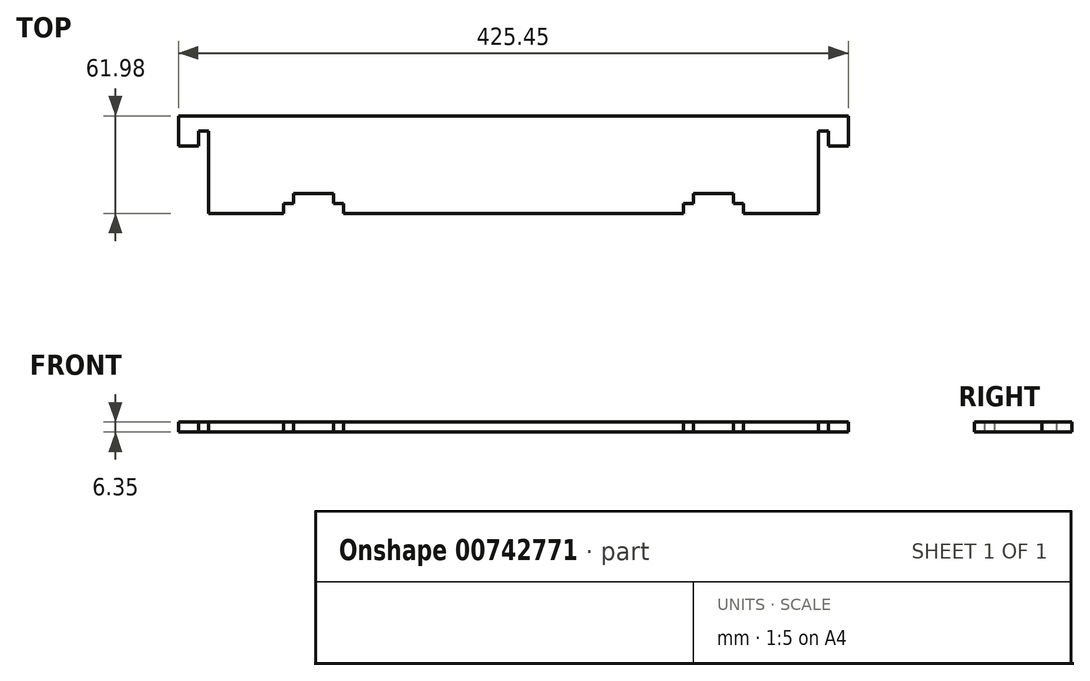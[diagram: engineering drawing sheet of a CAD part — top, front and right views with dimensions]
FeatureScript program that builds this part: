
annotation { "Feature Type Name" : "Feature", "Feature Type Description" : "" }
export const myFeature = defineFeature(function(context is Context, id is Id, definition is map)
    precondition{}
    {
        {
            var Q0;
            Q0=qCreatedBy(makeId("Top.planeOp"),FACE);
            var sketch = newSketch(context, id + "F0", { "sketchPlane" : qUnion([Q0])});
            skLineSegment(sketch, "E0.top", {"start": v(-116.14, -61.98) * mm, "end": v(-68.51, -61.98) * mm});
            skLineSegment(sketch, "E0.left", {"start": v(-116.14, 0) * mm, "end": v(-116.14, -61.98) * mm});
            skLineSegment(sketch, "E0.right", {"start": v(271.21, 0) * mm, "end": v(271.21, -61.98) * mm});
            skLineSegment(sketch, "E1.top", {"start": v(-68.51, -55.63) * mm, "end": v(-62.16, -55.63) * mm});
            skLineSegment(sketch, "E1.left", {"start": v(-68.51, -61.98) * mm, "end": v(-68.51, -55.63) * mm});
            skLineSegment(sketch, "E1.right", {"start": v(-30.41, -61.98) * mm, "end": v(-30.41, -55.63) * mm});
            skLineSegment(sketch, "E2.bottom", {"start": v(185.49, -55.63) * mm, "end": v(191.84, -55.63) * mm});
            skLineSegment(sketch, "E2.left", {"start": v(185.49, -55.63) * mm, "end": v(185.49, -61.98) * mm});
            skLineSegment(sketch, "E2.right", {"start": v(223.59, -55.63) * mm, "end": v(223.59, -61.98) * mm});
            skLineSegment(sketch, "E3.top", {"start": v(191.84, -49.28) * mm, "end": v(217.24, -49.28) * mm});
            skLineSegment(sketch, "E3.left", {"start": v(191.84, -55.63) * mm, "end": v(191.84, -49.28) * mm});
            skLineSegment(sketch, "E3.right", {"start": v(217.24, -55.63) * mm, "end": v(217.24, -49.28) * mm});
            skLineSegment(sketch, "E4.top", {"start": v(-62.16, -49.28) * mm, "end": v(-36.76, -49.28) * mm});
            skLineSegment(sketch, "E4.left", {"start": v(-62.16, -55.63) * mm, "end": v(-62.16, -49.28) * mm});
            skLineSegment(sketch, "E4.right", {"start": v(-36.76, -55.63) * mm, "end": v(-36.76, -49.28) * mm});
            skLineSegment(sketch, "E5.trimOffspring", {"start": v(-36.76, -55.63) * mm, "end": v(-30.41, -55.63) * mm});
            skLineSegment(sketch, "E6.trimOffspring", {"start": v(217.24, -55.63) * mm, "end": v(223.59, -55.63) * mm});
            skLineSegment(sketch, "E7.trimOffspring", {"start": v(223.59, -61.98) * mm, "end": v(271.21, -61.98) * mm});
            skLineSegment(sketch, "E8.trimOffspring", {"start": v(-116.14, 0) * mm, "end": v(271.21, 0) * mm});
            skLineSegment(sketch, "E9.trimOffspring", {"start": v(-30.41, -61.98) * mm, "end": v(185.49, -61.98) * mm});
            skSolve(sketch);
        }
        {
            var Q0;
            Q0=qSketchRegion(id+"F0",true);
            extrude(context, id + "F1", {"entities" : qUnion([Q0]), "depth" : 6.35 * mm, "offsetDistance" : 25.4 * mm});
        }
        {
            var Q0;
            Q0=makeQuery(id+"F1.opExtrude","CAP_FACE",FACE,{"disambiguationData":[OSD([sQuery(id+"F0.wireOp",EDGE,"E0.bottom"),sQuery(id+"F0.wireOp",EDGE,"E0.top"),sQuery(id+"F0.wireOp",EDGE,"E0.left"),sQuery(id+"F0.wireOp",EDGE,"E0.right"),sQuery(id+"F0.wireOp",EDGE,"E1.top"),sQuery(id+"F0.wireOp",EDGE,"E1.left"),sQuery(id+"F0.wireOp",EDGE,"E1.right"),sQuery(id+"F0.wireOp",EDGE,"E2.bottom"),sQuery(id+"F0.wireOp",EDGE,"E2.left"),sQuery(id+"F0.wireOp",EDGE,"E2.right"),sQuery(id+"F0.wireOp",EDGE,"E3.top"),sQuery(id+"F0.wireOp",EDGE,"E3.left"),sQuery(id+"F0.wireOp",EDGE,"E3.right"),sQuery(id+"F0.wireOp",EDGE,"E4.top"),sQuery(id+"F0.wireOp",EDGE,"E4.left"),sQuery(id+"F0.wireOp",EDGE,"E4.right"),sQuery(id+"F0.wireOp",EDGE,"E5.trimOffspring"),sQuery(id+"F0.wireOp",EDGE,"c7ddb3ed-293a-4f06-881b-95a2d0f9c08b.trimOffspring"),sQuery(id+"F0.wireOp",EDGE,"E6.trimOffspring"),sQuery(id+"F0.wireOp",EDGE,"E7.trimOffspring"),sQuery(id+"F0.wireOp",EDGE,"ymufXbJ0-fwJT-WBPx-Nqb6-yKuEAUtQnc4U.top"),sQuery(id+"F0.wireOp",EDGE,"ymufXbJ0-fwJT-WBPx-Nqb6-yKuEAUtQnc4U.left"),sQuery(id+"F0.wireOp",EDGE,"ymufXbJ0-fwJT-WBPx-Nqb6-yKuEAUtQnc4U.right"),sQuery(id+"F0.wireOp",EDGE,"E8.trimOffspring"),sQuery(id+"F0.wireOp",EDGE,"dkGOsc7M-t7lZ-icz2-LsQZ-ginpVgSsu80F.top"),sQuery(id+"F0.wireOp",EDGE,"dkGOsc7M-t7lZ-icz2-LsQZ-ginpVgSsu80F.left"),sQuery(id+"F0.wireOp",EDGE,"dkGOsc7M-t7lZ-icz2-LsQZ-ginpVgSsu80F.right"),sQuery(id+"F0.wireOp",EDGE,"E9.trimOffspring")])],"isStart":false});
            var sketch = newSketch(context, id + "F2", { "sketchPlane" : qUnion([Q0])});
            skLineSegment(sketch, "E10.bottom", {"start": v(271.21, 0) * mm, "end": v(290.26, 0) * mm});
            skLineSegment(sketch, "E10.top", {"start": v(277.56, -19.05) * mm, "end": v(290.26, -19.05) * mm});
            skLineSegment(sketch, "E10.left", {"start": v(271.21, 0) * mm, "end": v(271.21, -9.53) * mm});
            skLineSegment(sketch, "E10.right", {"start": v(290.26, 0) * mm, "end": v(290.26, -19.05) * mm});
            skLineSegment(sketch, "E11.top", {"start": v(271.21, -9.53) * mm, "end": v(277.56, -9.53) * mm});
            skLineSegment(sketch, "E11.right", {"start": v(277.56, -19.05) * mm, "end": v(277.56, -9.53) * mm});
            skLineSegment(sketch, "E12.bottom", {"start": v(-116.14, 0) * mm, "end": v(-135.19, 0) * mm});
            skLineSegment(sketch, "E12.top", {"start": v(-122.49, -19.05) * mm, "end": v(-135.19, -19.05) * mm});
            skLineSegment(sketch, "E12.left", {"start": v(-116.14, 0) * mm, "end": v(-116.14, -9.53) * mm});
            skLineSegment(sketch, "E12.right", {"start": v(-135.19, 0) * mm, "end": v(-135.19, -19.05) * mm});
            skLineSegment(sketch, "E13.top", {"start": v(-116.14, -9.53) * mm, "end": v(-122.49, -9.53) * mm});
            skLineSegment(sketch, "E13.right", {"start": v(-122.49, -19.05) * mm, "end": v(-122.49, -9.53) * mm});
            skSolve(sketch);
        }
        {
            var Q0;
            Q0=qSketchRegion(id+"F2",true);
            extrude(context, id + "F3", {"entities" : qUnion([Q0]), "operationType" : NewBodyOperationType.ADD, "oppositeDirection" : true, "depth" : 6.35 * mm, "offsetDistance" : 25.4 * mm});
        }
    });
